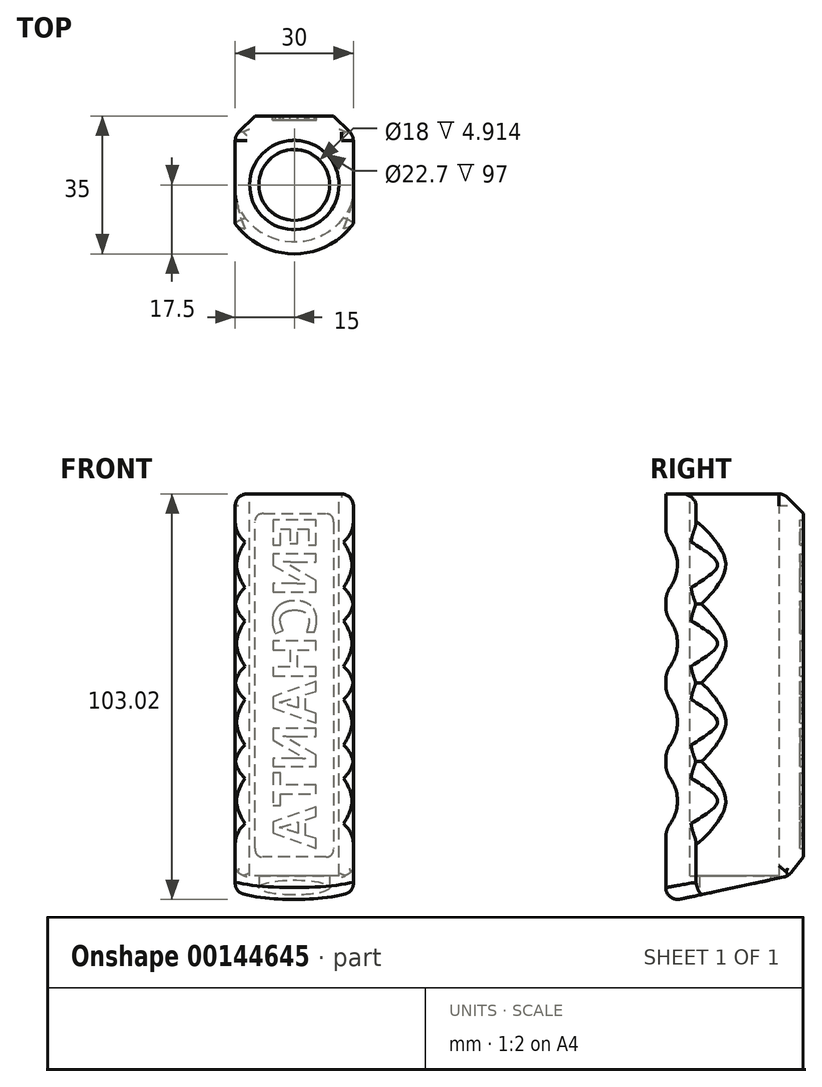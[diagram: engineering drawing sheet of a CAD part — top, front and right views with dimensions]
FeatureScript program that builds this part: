
annotation { "Feature Type Name" : "Feature", "Feature Type Description" : "" }
export const myFeature = defineFeature(function(context is Context, id is Id, definition is map)
    precondition{}
    {
        {
            var Q0;
            Q0=qCreatedBy(makeId("Top.planeOp"),FACE);
            var sketch = newSketch(context, id + "F0", { "sketchPlane" : qUnion([Q0])});
            skLineSegment(sketch, "E0.bottom", {"start": v(15, 17.5) * mm, "end": v(-15, 17.5) * mm});
            skLineSegment(sketch, "E0.top", {"start": v(15, -17.5) * mm, "end": v(-15, -17.5) * mm});
            skLineSegment(sketch, "E0.left", {"start": v(15, 17.5) * mm, "end": v(15, -17.5) * mm});
            skLineSegment(sketch, "E0.right", {"start": v(-15, 17.5) * mm, "end": v(-15, -17.5) * mm});
            skPoint(sketch, "E0.middle", {"position": v(0, 0) * mm});
            skSolve(sketch);
        }
        {
            var Q0;
            Q0 = qSketchRegion(id + "F0", true);
            extrude(context, id + "F1", {"entities" : qUnion([Q0]), "depth" : 100 * mm, "hasSecondDirection" : true, "secondDirectionOppositeDirection" : true, "secondDirectionDepth" : 5 * mm});
        }
        {
            var Q0;
            Q0=makeQuery(id+"F1.opExtrude","CAP_FACE",FACE,{"disambiguationData":[OSD([sQuery(id+"F0.wireOp",EDGE,"E0.bottom"),sQuery(id+"F0.wireOp",EDGE,"E0.top"),sQuery(id+"F0.wireOp",EDGE,"E0.left"),sQuery(id+"F0.wireOp",EDGE,"E0.right")])],"isStart":true});
            var sketch = newSketch(context, id + "F2", { "sketchPlane" : qUnion([Q0])});
            skCircle(sketch, "E1", {"center": v(0, 0) * mm, "radius": 9 * mm});
            skSolve(sketch);
        }
        {
            var Q0;
            Q0 = qSketchRegion(id + "F2", true);
            extrude(context, id + "F3", {"entities" : qUnion([Q0]), "operationType" : NewBodyOperationType.REMOVE, "oppositeDirection" : true, "depth" : 25 * mm});
        }
        {
            var Q0;
            Q0=makeQuery(id+"F1.opExtrude","CAP_FACE",FACE,{"disambiguationData":[OSD([sQuery(id+"F0.wireOp",EDGE,"E0.bottom"),sQuery(id+"F0.wireOp",EDGE,"E0.top"),sQuery(id+"F0.wireOp",EDGE,"E0.left"),sQuery(id+"F0.wireOp",EDGE,"E0.right")])],"isStart":false});
            var sketch = newSketch(context, id + "F4", { "sketchPlane" : qUnion([Q0])});
            skCircle(sketch, "E2.converted", {"center": v(0, 0) * mm, "radius": 11.35 * mm});
            skSolve(sketch);
        }
        {
            var Q0;
            Q0 = qSketchRegion(id + "F4", true);
            extrude(context, id + "F5", {"entities" : qUnion([Q0]), "operationType" : NewBodyOperationType.REMOVE, "oppositeDirection" : true, "depth" : 97 * mm});
        }
        {
            var Q0;
            Q0=qCreatedBy(makeId("Right.planeOp"),FACE);
            var sketch = newSketch(context, id + "F6", { "sketchPlane" : qUnion([Q0])});
            skLineSegment(sketch, "E3", {"start": v(0.06, 88) * mm, "end": v(0, 88) * mm, "construction": true});
            skLineSegment(sketch, "E4", {"start": v(-10.43, 22) * mm, "end": v(-28.15, 22) * mm, "construction": true});
            skPoint(sketch, "E5.visualSharp", {"position": v(-10.43, 22) * mm});
            skArc(sketch, "E5.filletArc", {"start": v(-17.5, 14.93) * mm, "mid": v(-14.57, 22) * mm, "end": v(-17.5, 29.07) * mm});
            skArc(sketch, "E6.0.1.0", {"start": v(-17.5, 34.93) * mm, "mid": v(-14.57, 42) * mm, "end": v(-17.5, 49.07) * mm});
            skArc(sketch, "E6.0.2.0", {"start": v(-17.5, 54.93) * mm, "mid": v(-14.57, 62) * mm, "end": v(-17.5, 69.07) * mm});
            skArc(sketch, "E6.0.3.0", {"start": v(-17.5, 74.93) * mm, "mid": v(-14.57, 82) * mm, "end": v(-17.5, 89.07) * mm});
            skLineSegment(sketch, "E7", {"start": v(-34.18, 7.03) * mm, "end": v(-34.18, 94.6) * mm});
            skPoint(sketch, "E8.orphan", {"position": v(-17.5, 100) * mm});
            skPoint(sketch, "E9.orphan", {"position": v(-17.5, -5.81) * mm});
            skLineSegment(sketch, "E10", {"start": v(-17.5, 74.93) * mm, "end": v(-17.5, 69.07) * mm});
            skLineSegment(sketch, "E11", {"start": v(-17.5, 54.93) * mm, "end": v(-17.5, 49.07) * mm});
            skLineSegment(sketch, "E12", {"start": v(-17.5, 34.93) * mm, "end": v(-17.5, 29.07) * mm});
            skLineSegment(sketch, "E13", {"start": v(-17.5, 14.93) * mm, "end": v(-17.5, -5.81) * mm});
            skLineSegment(sketch, "E14", {"start": v(-17.5, 89.07) * mm, "end": v(-17.5, 100) * mm});
            skLineSegment(sketch, "E15", {"start": v(-34.18, 100) * mm, "end": v(-34.18, 94.6) * mm});
            skLineSegment(sketch, "E16", {"start": v(-34.18, 100) * mm, "end": v(-17.5, 100) * mm});
            skLineSegment(sketch, "E17", {"start": v(-17.5, -5.81) * mm, "end": v(-34.18, -5.81) * mm});
            skLineSegment(sketch, "E18", {"start": v(-34.18, -5.81) * mm, "end": v(-34.18, 7.03) * mm});
            skLineSegment(sketch, "E19", {"start": v(1, 0) * mm, "end": v(1, 99.86) * mm, "construction": true});
            skSolve(sketch);
        }
        {
            var Q0;
            Q0 = qSketchRegion(id + "F6", true);
            var Q1;
            Q1=sQuery(id+"F6.wireOp",EDGE,"E19");
            revolve(context, id + "F7", {"operationType" : NewBodyOperationType.REMOVE, "entities" : qUnion([Q0]), "axis" : qUnion([Q1]), "revolveType" : RevolveType.SYMMETRIC, "angle" : 180 * degree});
        }
        {
            var Q0;
            Q0=qCreatedBy(makeId("Right.planeOp"),FACE);
            var sketch = newSketch(context, id + "F8", { "sketchPlane" : qUnion([Q0])});
            skLineSegment(sketch, "E20", {"start": v(31.28, 6.65) * mm, "end": v(31.28, -5.8) * mm});
            skLineSegment(sketch, "E21", {"start": v(31.28, -5.8) * mm, "end": v(-27.3, -5.8) * mm});
            skLineSegment(sketch, "E22", {"start": v(-27.3, -5.8) * mm, "end": v(31.28, 6.65) * mm});
            skSolve(sketch);
        }
        {
            var Q0;
            Q0 = qSketchRegion(id + "F8", true);
            extrude(context, id + "F9", {"entities" : qUnion([Q0]), "operationType" : NewBodyOperationType.REMOVE, "endBound" : BoundingType.THROUGH_ALL, "oppositeDirection" : true, "depth" : 25 * mm, "hasSecondDirection" : true, "secondDirectionBound" : SecondDirectionBoundingType.THROUGH_ALL, "secondDirectionOppositeDirection" : false, "secondDirectionDepth" : 25 * mm});
        }
        {
            var Q0;
            Q0=makeQuery(id+"F1.opExtrude","SWEPT_FACE",FACE,{"disambiguationData":[OSD([sQuery(id+"F0.wireOp",EDGE,"E0.bottom")])]});
            var sketch = newSketch(context, id + "F10", { "sketchPlane" : qUnion([Q0])});
            skText(sketch, "E23", { "text": "ENCHANTA", "fontName": "OpenSans-Bold.ttf"});
            skLineSegment(sketch, "E24.0", {"start": v(-15, 100) * mm, "end": v(-15, 3.72) * mm, "construction": true});
            skLineSegment(sketch, "E25.0", {"start": v(-15, 100) * mm, "end": v(15, 100) * mm});
            const initialGuessF10  = {"E23": [-0.0055, 0.09473, 0, -1, 0.011]};
            skSetInitialGuess(sketch, initialGuessF10);
            skSolve(sketch);
        }
        {
            var Q0;
            Q0 = qSketchRegion(id + "F10", true);
            extrude(context, id + "F11", {"entities" : qUnion([Q0]), "operationType" : NewBodyOperationType.REMOVE, "oppositeDirection" : true, "depth" : 1 * mm});
        }
        {
            var Q0;
            Q0=makeQuery(id+"F1.opExtrude","SWEPT_EDGE",EDGE,{"disambiguationData":[OSD([sQuery(id+"F0.wireOp",EDGE,"E0.bottom"),sQuery(id+"F0.wireOp",EDGE,"E0.right")])]});
            var Q1;
            Q1=makeQuery(id+"F1.opExtrude","SWEPT_EDGE",EDGE,{"disambiguationData":[OSD([sQuery(id+"F0.wireOp",EDGE,"E0.bottom"),sQuery(id+"F0.wireOp",EDGE,"E0.left")])]});
            var Q2;
            Q2=makeQuery(id+"F1.opExtrude","CAP_EDGE",EDGE,{"disambiguationData":[OSD([sQuery(id+"F0.wireOp",EDGE,"E0.bottom")])],"isStart":false});
            var Q3;
            Q3=makeQuery(id+"F9.boolean.opBoolean","INTERSECT",EDGE,{"derivedFrom":[makeQuery(id+"F1.opExtrude","SWEPT_FACE",FACE,{"disambiguationData":[OSD([sQuery(id+"F0.wireOp",EDGE,"E0.bottom")])]}),makeQuery(id+"F9.opExtrude","SWEPT_FACE",FACE,{"disambiguationData":[OSD([sQuery(id+"F8.wireOp",EDGE,"E22")])]})]});
            chamfer(context, id + "F12", {"entities" : qUnion([Q0, Q1, Q2, Q3]), "width" : 5 * mm, "tangentPropagation" : true});
        }
        {
            var Q0;
            Q0=makeQuery(id+"F1.opExtrude","CAP_EDGE",EDGE,{"disambiguationData":[OSD([sQuery(id+"F0.wireOp",EDGE,"E0.left")])],"isStart":false});
            var Q1;
            Q1=makeQuery(id+"F7.boolean.opBoolean","COPY",EDGE,{"derivedFrom":makeQuery(id+"F7.opRevolve","SWEPT_EDGE",EDGE,{"disambiguationData":[OSD([sQuery(id+"F6.wireOp",EDGE,"E14"),sQuery(id+"F6.wireOp",EDGE,"E16")])]})});
            var Q2;
            Q2=makeQuery(id+"F1.opExtrude","CAP_EDGE",EDGE,{"disambiguationData":[OSD([sQuery(id+"F0.wireOp",EDGE,"E0.right")])],"isStart":false});
            fillet(context, id + "F13", {"entities" : qUnion([Q0, Q1, Q2]), "radius" : 3 * mm, "tangentPropagation" : true, "allowEdgeOverflow" : false});
        }
        {
            var Q0;
            Q0=makeQuery(id+"F7.boolean.opBoolean","COPY",FACE,{"derivedFrom":makeQuery(id+"F7.opRevolve","SWEPT_FACE",FACE,{"disambiguationData":[OSD([sQuery(id+"F6.wireOp",EDGE,"E6.0.3.0")])]})});
            var Q1;
            Q1=makeQuery(id+"F7.boolean.opBoolean","COPY",FACE,{"derivedFrom":makeQuery(id+"F7.opRevolve","SWEPT_FACE",FACE,{"disambiguationData":[OSD([sQuery(id+"F6.wireOp",EDGE,"E6.0.2.0")])]})});
            var Q2;
            Q2=makeQuery(id+"F7.boolean.opBoolean","COPY",FACE,{"derivedFrom":makeQuery(id+"F7.opRevolve","SWEPT_FACE",FACE,{"disambiguationData":[OSD([sQuery(id+"F6.wireOp",EDGE,"E5.filletArc")])]})});
            var Q3;
            Q3=makeQuery(id+"F7.boolean.opBoolean","COPY",FACE,{"derivedFrom":makeQuery(id+"F7.opRevolve","SWEPT_FACE",FACE,{"disambiguationData":[OSD([sQuery(id+"F6.wireOp",EDGE,"E6.0.1.0")])]})});
            fillet(context, id + "F14", {"entities" : qUnion([Q0, Q1, Q2, Q3]), "radius" : 6 * mm, "tangentPropagation" : true, "allowEdgeOverflow" : false});
        }
        {
            var Q0;
            Q0=makeQuery(id+"F9.boolean.opBoolean","INTERSECT",EDGE,{"derivedFrom":[makeQuery(id+"F7.boolean.opBoolean","COPY",FACE,{"derivedFrom":makeQuery(id+"F7.opRevolve","SWEPT_FACE",FACE,{"disambiguationData":[OSD([sQuery(id+"F6.wireOp",EDGE,"E13")])]})}),makeQuery(id+"F9.opExtrude","SWEPT_FACE",FACE,{"disambiguationData":[OSD([sQuery(id+"F8.wireOp",EDGE,"E22")])]})]});
            var Q1;
            Q1=makeQuery(id+"F9.boolean.opBoolean","INTERSECT",EDGE,{"derivedFrom":[makeQuery(id+"F1.opExtrude","SWEPT_FACE",FACE,{"disambiguationData":[OSD([sQuery(id+"F0.wireOp",EDGE,"E0.right")])]}),makeQuery(id+"F9.opExtrude","SWEPT_FACE",FACE,{"disambiguationData":[OSD([sQuery(id+"F8.wireOp",EDGE,"E22")])]})]});
            var Q2;
            Q2=makeQuery(id+"F9.boolean.opBoolean","INTERSECT",EDGE,{"derivedFrom":[makeQuery(id+"F1.opExtrude","SWEPT_FACE",FACE,{"disambiguationData":[OSD([sQuery(id+"F0.wireOp",EDGE,"E0.left")])]}),makeQuery(id+"F9.opExtrude","SWEPT_FACE",FACE,{"disambiguationData":[OSD([sQuery(id+"F8.wireOp",EDGE,"E22")])]})]});
            var Q3;
            {var subQ0=sQuery(id+"F0.wireOp",EDGE,"E0.bottom");Q3=makeQuery(id+"F12.opChamfer","BLEND_EDGE",EDGE,{"blendedFrom":[makeQuery(id+"F1.opExtrude","SWEPT_EDGE",EDGE,{"disambiguationData":[OSD([subQ0,sQuery(id+"F0.wireOp",EDGE,"E0.right")])]}),makeQuery(id+"F9.boolean.opBoolean","INTERSECT",EDGE,{"derivedFrom":[makeQuery(id+"F1.opExtrude","SWEPT_FACE",FACE,{"disambiguationData":[OSD([subQ0])]}),makeQuery(id+"F9.opExtrude","SWEPT_FACE",FACE,{"disambiguationData":[OSD([sQuery(id+"F8.wireOp",EDGE,"E22")])]})]})],"blendedInto":[]});}
            var Q4;
            {var subQ0=sQuery(id+"F0.wireOp",EDGE,"E0.bottom");Q4=makeQuery(id+"F12.opChamfer","BLEND_EDGE",EDGE,{"blendedFrom":[makeQuery(id+"F1.opExtrude","SWEPT_EDGE",EDGE,{"disambiguationData":[OSD([subQ0,sQuery(id+"F0.wireOp",EDGE,"E0.left")])]}),makeQuery(id+"F9.boolean.opBoolean","INTERSECT",EDGE,{"derivedFrom":[makeQuery(id+"F1.opExtrude","SWEPT_FACE",FACE,{"disambiguationData":[OSD([subQ0])]}),makeQuery(id+"F9.opExtrude","SWEPT_FACE",FACE,{"disambiguationData":[OSD([sQuery(id+"F8.wireOp",EDGE,"E22")])]})]})],"blendedInto":[]});}
            var Q5;
            {var subQ0=sQuery(id+"F0.wireOp",EDGE,"E0.left");Q5=makeQuery(id+"F12.opChamfer","BLEND_EDGE",EDGE,{"blendedFrom":[makeQuery(id+"F1.opExtrude","SWEPT_EDGE",EDGE,{"disambiguationData":[OSD([sQuery(id+"F0.wireOp",EDGE,"E0.bottom"),subQ0])]}),makeQuery(id+"F1.opExtrude","SWEPT_FACE",FACE,{"disambiguationData":[OSD([subQ0])]})],"blendedInto":[makeQuery(id+"F1.opExtrude","SWEPT_FACE",FACE,{"disambiguationData":[OSD([subQ0])]})]});}
            var Q6;
            {var subQ0=sQuery(id+"F0.wireOp",EDGE,"E0.right");Q6=makeQuery(id+"F12.opChamfer","BLEND_EDGE",EDGE,{"blendedFrom":[makeQuery(id+"F1.opExtrude","SWEPT_EDGE",EDGE,{"disambiguationData":[OSD([sQuery(id+"F0.wireOp",EDGE,"E0.bottom"),subQ0])]}),makeQuery(id+"F1.opExtrude","SWEPT_FACE",FACE,{"disambiguationData":[OSD([subQ0])]})],"blendedInto":[makeQuery(id+"F1.opExtrude","SWEPT_FACE",FACE,{"disambiguationData":[OSD([subQ0])]})]});}
            var Q7;
            {var subQ0=makeQuery(id+"F9.opExtrude","SWEPT_FACE",FACE,{"disambiguationData":[OSD([sQuery(id+"F8.wireOp",EDGE,"E22")])]});Q7=makeQuery(id+"F12.opChamfer","BLEND_EDGE",EDGE,{"blendedFrom":[makeQuery(id+"F9.boolean.opBoolean","INTERSECT",EDGE,{"derivedFrom":[makeQuery(id+"F1.opExtrude","SWEPT_FACE",FACE,{"disambiguationData":[OSD([sQuery(id+"F0.wireOp",EDGE,"E0.bottom")])]}),subQ0]}),makeQuery(id+"F9.boolean.opBoolean","COPY",FACE,{"derivedFrom":subQ0})],"blendedInto":[makeQuery(id+"F9.boolean.opBoolean","COPY",FACE,{"derivedFrom":subQ0})]});}
            var Q8;
            {var subQ0=sQuery(id+"F0.wireOp",EDGE,"E0.bottom");Q8=makeQuery(id+"F12.opChamfer","BLEND_EDGE",EDGE,{"blendedFrom":[makeQuery(id+"F1.opExtrude","CAP_EDGE",EDGE,{"disambiguationData":[OSD([subQ0])],"isStart":false}),makeQuery(id+"F1.opExtrude","CAP_FACE",FACE,{"disambiguationData":[OSD([subQ0,sQuery(id+"F0.wireOp",EDGE,"E0.top"),sQuery(id+"F0.wireOp",EDGE,"E0.left"),sQuery(id+"F0.wireOp",EDGE,"E0.right")])],"isStart":false})],"blendedInto":[makeQuery(id+"F1.opExtrude","CAP_FACE",FACE,{"disambiguationData":[OSD([subQ0,sQuery(id+"F0.wireOp",EDGE,"E0.top"),sQuery(id+"F0.wireOp",EDGE,"E0.left"),sQuery(id+"F0.wireOp",EDGE,"E0.right")])],"isStart":false})]});}
            var Q9;
            {var subQ0=sQuery(id+"F0.wireOp",EDGE,"E0.bottom");Q9=makeQuery(id+"F12.opChamfer","BLEND_EDGE",EDGE,{"blendedFrom":[makeQuery(id+"F1.opExtrude","CAP_EDGE",EDGE,{"disambiguationData":[OSD([subQ0])],"isStart":false}),makeQuery(id+"F1.opExtrude","SWEPT_EDGE",EDGE,{"disambiguationData":[OSD([subQ0,sQuery(id+"F0.wireOp",EDGE,"E0.left")])]})],"blendedInto":[]});}
            var Q10;
            {var subQ0=sQuery(id+"F0.wireOp",EDGE,"E0.bottom");Q10=makeQuery(id+"F12.opChamfer","BLEND_EDGE",EDGE,{"blendedFrom":[makeQuery(id+"F1.opExtrude","CAP_EDGE",EDGE,{"disambiguationData":[OSD([subQ0])],"isStart":false}),makeQuery(id+"F1.opExtrude","SWEPT_EDGE",EDGE,{"disambiguationData":[OSD([subQ0,sQuery(id+"F0.wireOp",EDGE,"E0.right")])]})],"blendedInto":[]});}
            fillet(context, id + "F15", {"entities" : qUnion([Q0, Q1, Q2, Q3, Q4, Q5, Q6, Q7, Q8, Q9, Q10]), "radius" : 3 * mm, "tangentPropagation" : true, "allowEdgeOverflow" : false});
        }
    });
